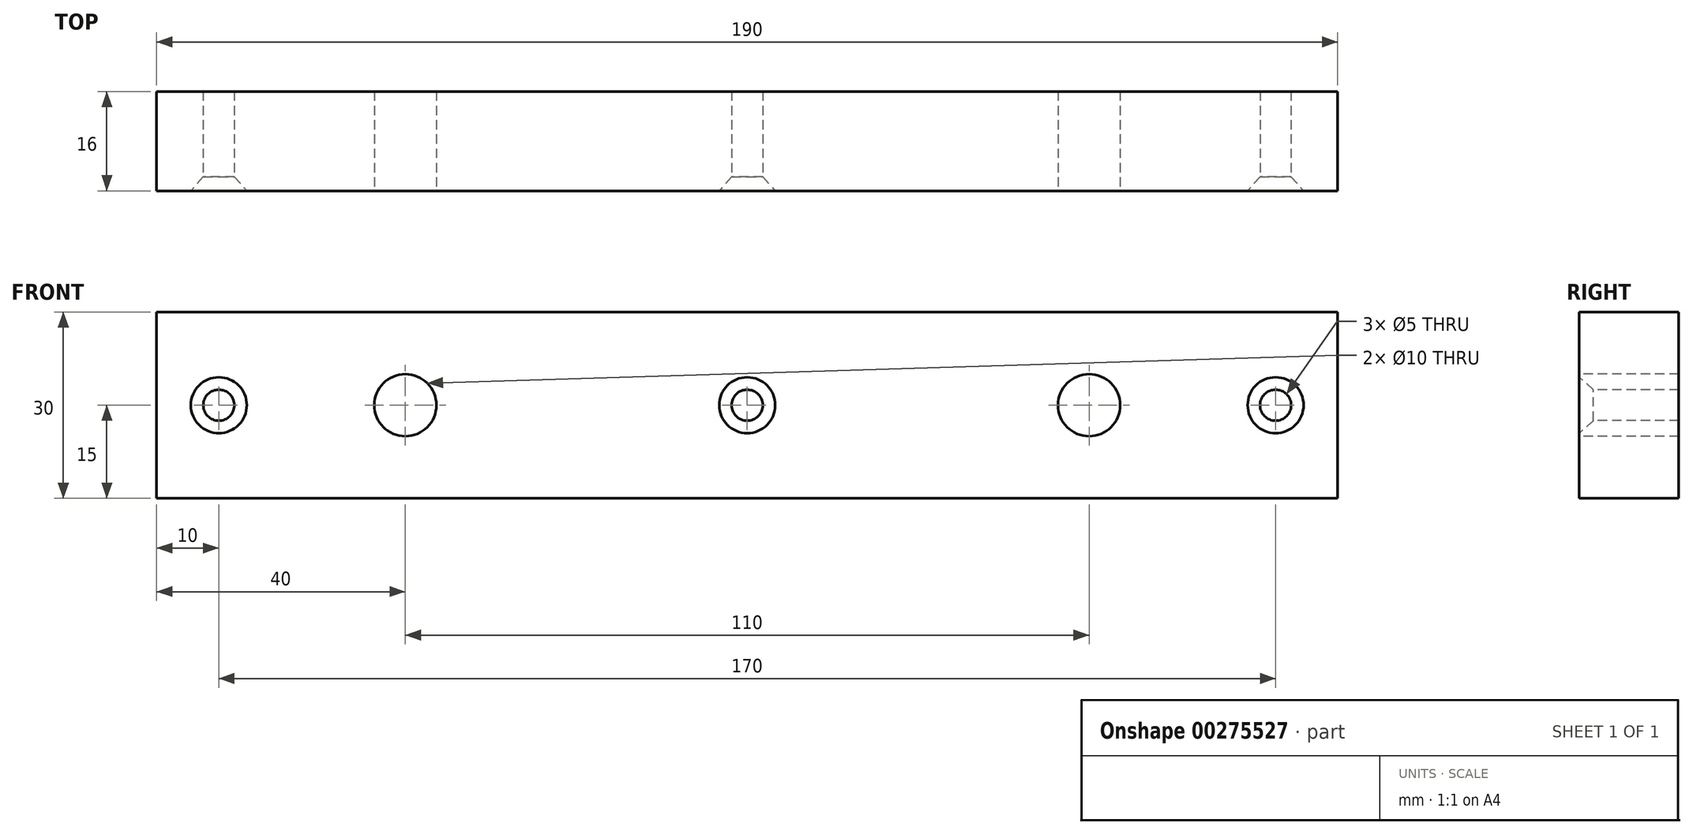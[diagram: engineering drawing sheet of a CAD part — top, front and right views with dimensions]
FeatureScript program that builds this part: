
annotation { "Feature Type Name" : "Feature", "Feature Type Description" : "" }
export const myFeature = defineFeature(function(context is Context, id is Id, definition is map)
    precondition{}
    {
        {
            var Q0;
            Q0=qCreatedBy(makeId("Front.planeOp"),FACE);
            var sketch = newSketch(context, id + "F0", { "sketchPlane" : qUnion([Q0])});
            skLineSegment(sketch, "E0.bottom", {"start": v(0, 0) * mm, "end": v(190, 0) * mm});
            skLineSegment(sketch, "E0.top", {"start": v(0, -30) * mm, "end": v(190, -30) * mm});
            skLineSegment(sketch, "E0.left", {"start": v(0, 0) * mm, "end": v(0, -30) * mm});
            skLineSegment(sketch, "E0.right", {"start": v(190, 0) * mm, "end": v(190, -30) * mm});
            skSolve(sketch);
        }
        {
            var Q0;
            Q0=makeQuery(id+"F0.imprint","IMPRINT",FACE,{"disambiguationData":[TD([[makeQuery(id+"F0.imprint","IMPRINT",EDGE,{"derivedFrom":sQuery(id+"F0.wireOp",EDGE,"E0.bottom")}),-1.0]])]});
            extrude(context, id + "F1", {"entities" : qUnion([Q0]), "depth" : 16 * mm});
        }
        {
            var Q0;
            Q0=makeQuery(id+"F1.opExtrude","CAP_FACE",FACE,{"disambiguationData":[OSD([sQuery(id+"F0.wireOp",EDGE,"E0.bottom"),sQuery(id+"F0.wireOp",EDGE,"E0.top"),sQuery(id+"F0.wireOp",EDGE,"E0.left"),sQuery(id+"F0.wireOp",EDGE,"E0.right")])],"isStart":false});
            var sketch = newSketch(context, id + "F2", { "sketchPlane" : qUnion([Q0])});
            skPoint(sketch, "E1", {"position": v(10, -15) * mm});
            skPoint(sketch, "E2", {"position": v(40, -15) * mm});
            skPoint(sketch, "E3", {"position": v(95, -15) * mm});
            skPoint(sketch, "E4", {"position": v(156, -52.79) * mm});
            skPoint(sketch, "E5", {"position": v(180, -15) * mm});
            skSolve(sketch);
        }
        {
            var Q0;
            Q0=sQuery(id+"F2.wireOp",VERTEX,"E1");
            var Q1;
            Q1=sQuery(id+"F2.wireOp",VERTEX,"E3");
            var Q2;
            Q2=sQuery(id+"F2.wireOp",VERTEX,"E5");
            var Q3;
            Q3=sQuery(id+"F2.wireOp",VERTEX,"E5");
            var Q4;
            Q4=makeQuery(id+"F1.opExtrude","SWEPT_BODY",BODY,{"disambiguationData":[OSD([sQuery(id+"F0.wireOp",EDGE,"E0.bottom"),sQuery(id+"F0.wireOp",EDGE,"E0.top"),sQuery(id+"F0.wireOp",EDGE,"E0.left"),sQuery(id+"F0.wireOp",EDGE,"E0.right")])]});
            hole(context, id + "F3", {"style" : HoleStyle.C_SINK, "endStyle" : HoleEndStyle.THROUGH, "holeDiameter" : 5 * mm, "cSinkDiameter" : 9 * mm, "cSinkAngle" : 82 * degree, "tappedDepth" : 50 * mm, "tapClearance" : 3, "locations" : qUnion([Q0, Q1, Q2, Q3]), "scope" : qUnion([Q4])});
        }
        {
            var Q0;
            Q0=sQuery(id+"F2.wireOp",VERTEX,"E2");
            var Q1;
            Q1=sQuery(id+"F2.wireOp",VERTEX,"E4");
            var Q2;
            Q2=makeQuery(id+"F1.opExtrude","SWEPT_BODY",BODY,{"disambiguationData":[OSD([sQuery(id+"F0.wireOp",EDGE,"E0.bottom"),sQuery(id+"F0.wireOp",EDGE,"E0.top"),sQuery(id+"F0.wireOp",EDGE,"E0.left"),sQuery(id+"F0.wireOp",EDGE,"E0.right")])]});
            hole(context, id + "F4", {"style" : HoleStyle.SIMPLE, "endStyle" : HoleEndStyle.THROUGH, "holeDiameter" : 10 * mm, "tappedDepth" : 50 * mm, "tapClearance" : 3, "locations" : qUnion([Q0, Q1]), "scope" : qUnion([Q2])});
        }
        {
            var Q0;
            Q0=makeQuery(id+"F2.imprint","IMPRINT",FACE,{"disambiguationData":[TD([[makeQuery(id+"F2.imprint","IMPRINT",EDGE,{"derivedFrom":makeQuery(id+"F1.opExtrude","CAP_EDGE",EDGE,{"disambiguationData":[OSD([sQuery(id+"F0.wireOp",EDGE,"E0.bottom")])],"isStart":false})}),-1.0]])]});
            var sketch = newSketch(context, id + "F5", { "sketchPlane" : qUnion([Q0])});
            skPoint(sketch, "E6", {"position": v(150, -15) * mm});
            skSolve(sketch);
        }
        {
            var Q0;
            Q0=sQuery(id+"F5.wireOp",VERTEX,"E6");
            var Q1;
            Q1=makeQuery(id+"F1.opExtrude","SWEPT_BODY",BODY,{"disambiguationData":[OSD([sQuery(id+"F0.wireOp",EDGE,"E0.bottom"),sQuery(id+"F0.wireOp",EDGE,"E0.top"),sQuery(id+"F0.wireOp",EDGE,"E0.left"),sQuery(id+"F0.wireOp",EDGE,"E0.right")])]});
            hole(context, id + "F6", {"style" : HoleStyle.SIMPLE, "endStyle" : HoleEndStyle.THROUGH, "holeDiameter" : 10 * mm, "tappedDepth" : 50 * mm, "tapClearance" : 3, "locations" : qUnion([Q0]), "scope" : qUnion([Q1])});
        }
    });
